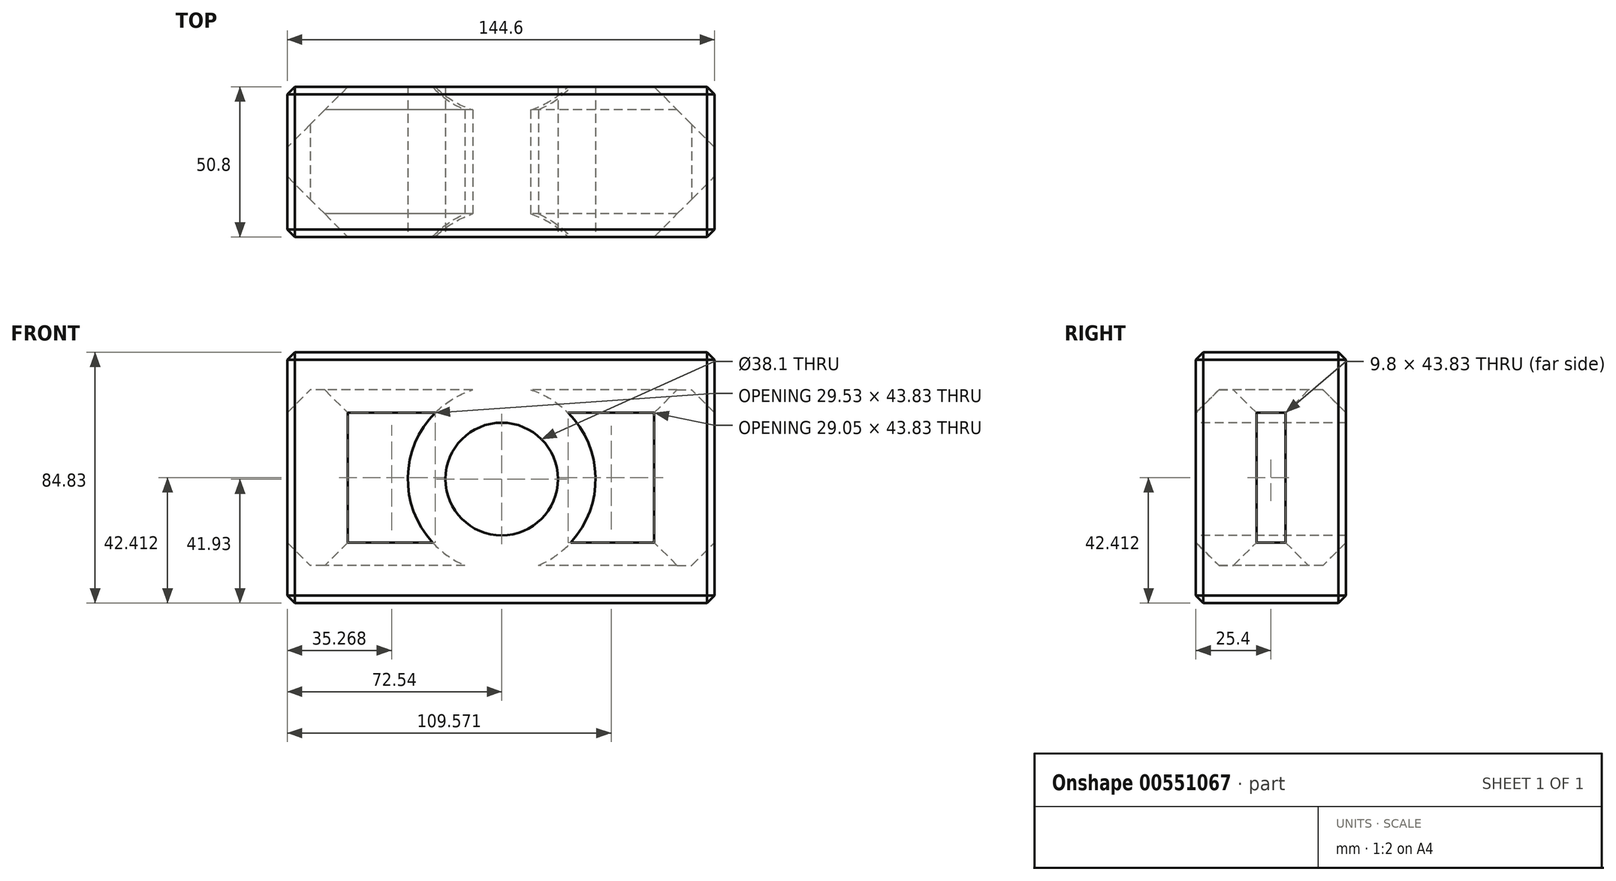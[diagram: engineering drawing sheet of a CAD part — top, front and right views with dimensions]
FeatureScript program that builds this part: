
annotation { "Feature Type Name" : "Feature", "Feature Type Description" : "" }
export const myFeature = defineFeature(function(context is Context, id is Id, definition is map)
    precondition{}
    {
        {
            var Q0;
            Q0=qCreatedBy(makeId("Front.planeOp"),FACE);
            var sketch = newSketch(context, id + "F0", { "sketchPlane" : qUnion([Q0])});
            skLineSegment(sketch, "E0.bottom", {"start": v(-72.54, 42.9) * mm, "end": v(72.06, 42.9) * mm});
            skLineSegment(sketch, "E0.top", {"start": v(-72.54, -41.93) * mm, "end": v(72.06, -41.93) * mm});
            skLineSegment(sketch, "E0.left", {"start": v(-72.54, 42.9) * mm, "end": v(-72.54, -41.93) * mm});
            skLineSegment(sketch, "E0.right", {"start": v(72.06, 42.9) * mm, "end": v(72.06, -41.93) * mm});
            skSolve(sketch);
        }
        {
            var Q0;
            Q0 = qSketchRegion(id + "F0", true);
            var Q1;
            Q1=makeQuery(id+"F0.imprint","IMPRINT",FACE,{"disambiguationData":[TD([[makeQuery(id+"F0.imprint","IMPRINT",EDGE,{"derivedFrom":sQuery(id+"F0.wireOp",EDGE,"E0.bottom")}),-1.0]])]});
            extrude(context, id + "F1", {"entities" : qUnion([Q0, Q1]), "depth" : 50.8 * mm, "offsetDistance" : 25.4 * mm});
        }
        {
            var Q0;
            Q0=makeQuery(id+"F1.opExtrude","SWEPT_FACE",FACE,{"disambiguationData":[OSD([sQuery(id+"F0.wireOp",EDGE,"E0.bottom")])]});
            var Q1;
            Q1=makeQuery(id+"F1.opExtrude","CAP_FACE",FACE,{"disambiguationData":[OSD([sQuery(id+"F0.wireOp",EDGE,"E0.bottom"),sQuery(id+"F0.wireOp",EDGE,"E0.top"),sQuery(id+"F0.wireOp",EDGE,"E0.left"),sQuery(id+"F0.wireOp",EDGE,"E0.right")])],"isStart":false});
            var Q2;
            Q2=makeQuery(id+"F1.opExtrude","SWEPT_FACE",FACE,{"disambiguationData":[OSD([sQuery(id+"F0.wireOp",EDGE,"E0.left")])]});
            var Q3;
            Q3=makeQuery(id+"F1.opExtrude","SWEPT_FACE",FACE,{"disambiguationData":[OSD([sQuery(id+"F0.wireOp",EDGE,"E0.right")])]});
            var Q4;
            Q4=makeQuery(id+"F1.opExtrude","CAP_FACE",FACE,{"disambiguationData":[OSD([sQuery(id+"F0.wireOp",EDGE,"E0.bottom"),sQuery(id+"F0.wireOp",EDGE,"E0.top"),sQuery(id+"F0.wireOp",EDGE,"E0.left"),sQuery(id+"F0.wireOp",EDGE,"E0.right")])],"isStart":true});
            var Q5;
            Q5=makeQuery(id+"F1.opExtrude","SWEPT_FACE",FACE,{"disambiguationData":[OSD([sQuery(id+"F0.wireOp",EDGE,"E0.top")])]});
            chamfer(context, id + "F2", {"entities" : qUnion([Q0, Q1, Q2, Q3, Q4, Q5]), "width" : 2.54 * mm, "tangentPropagation" : true});
        }
        {
            var Q0;
            Q0=makeQuery(id+"F1.opExtrude","CAP_FACE",FACE,{"disambiguationData":[OSD([sQuery(id+"F0.wireOp",EDGE,"E0.bottom"),sQuery(id+"F0.wireOp",EDGE,"E0.top"),sQuery(id+"F0.wireOp",EDGE,"E0.left"),sQuery(id+"F0.wireOp",EDGE,"E0.right")])],"isStart":false});
            var sketch = newSketch(context, id + "F3", { "sketchPlane" : qUnion([Q0])});
            skPoint(sketch, "E1", {"position": v(0, 0) * mm});
            skSolve(sketch);
        }
        {
            var Q0;
            Q0=sQuery(id+"F3.wireOp",VERTEX,"E1");
            var Q1;
            Q1=makeQuery(id+"F1.opExtrude","SWEPT_BODY",BODY,{"disambiguationData":[OSD([sQuery(id+"F0.wireOp",EDGE,"E0.bottom"),sQuery(id+"F0.wireOp",EDGE,"E0.top"),sQuery(id+"F0.wireOp",EDGE,"E0.left"),sQuery(id+"F0.wireOp",EDGE,"E0.right")])]});
            hole(context, id + "F4", {"style" : HoleStyle.SIMPLE, "endStyle" : HoleEndStyle.THROUGH, "holeDiameter" : 38.1 * mm, "isTappedThrough" : true, "tappedDepth" : 12.7 * mm, "tapClearance" : 3, "locations" : qUnion([Q0]), "scope" : qUnion([Q1])});
        }
        {
            var Q0;
            Q0=makeQuery(id+"F1.opExtrude","SWEPT_FACE",FACE,{"disambiguationData":[OSD([sQuery(id+"F0.wireOp",EDGE,"E0.left")])]});
            var Q1;
            Q1=makeQuery(id+"F1.opExtrude","CAP_FACE",FACE,{"disambiguationData":[OSD([sQuery(id+"F0.wireOp",EDGE,"E0.bottom"),sQuery(id+"F0.wireOp",EDGE,"E0.top"),sQuery(id+"F0.wireOp",EDGE,"E0.left"),sQuery(id+"F0.wireOp",EDGE,"E0.right")])],"isStart":false});
            var Q2;
            Q2=makeQuery(id+"F1.opExtrude","CAP_FACE",FACE,{"disambiguationData":[OSD([sQuery(id+"F0.wireOp",EDGE,"E0.bottom"),sQuery(id+"F0.wireOp",EDGE,"E0.top"),sQuery(id+"F0.wireOp",EDGE,"E0.left"),sQuery(id+"F0.wireOp",EDGE,"E0.right")])],"isStart":true});
            var Q3;
            Q3=makeQuery(id+"F1.opExtrude","SWEPT_FACE",FACE,{"disambiguationData":[OSD([sQuery(id+"F0.wireOp",EDGE,"E0.right")])]});
            shell(context, id + "F5", {"entities" : qUnion([Q0, Q1, Q2, Q3]), "thickness" : 12.7 * mm});
        }
    });
